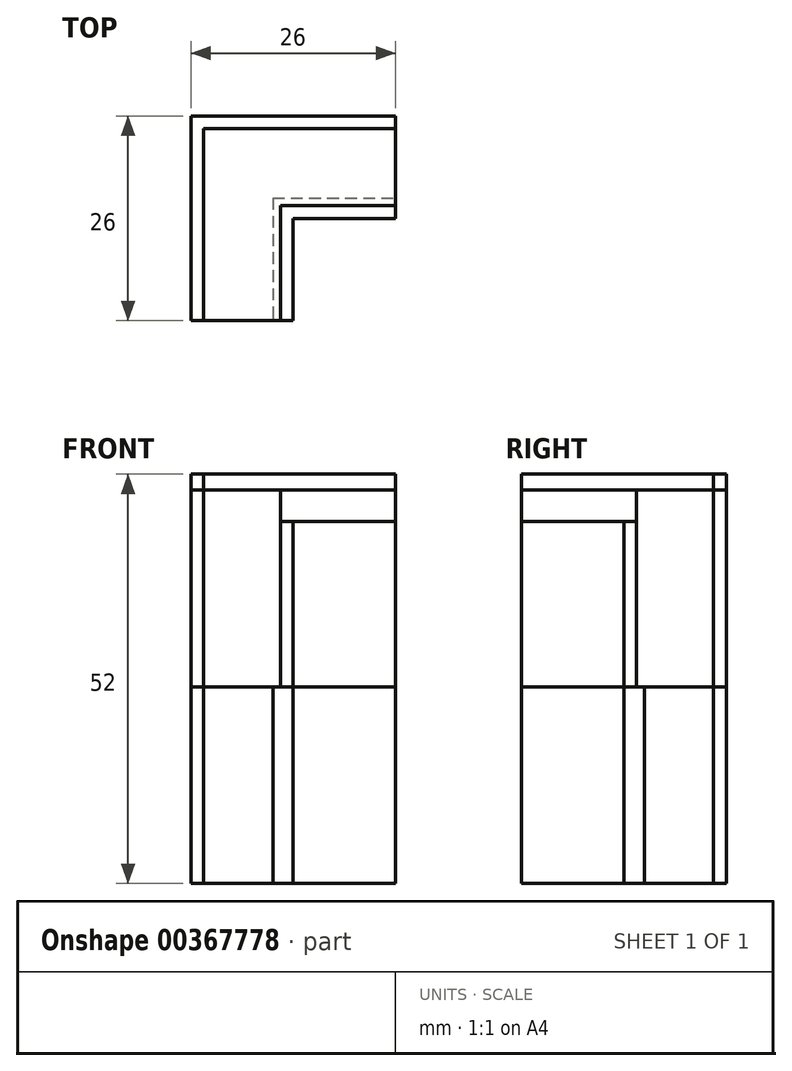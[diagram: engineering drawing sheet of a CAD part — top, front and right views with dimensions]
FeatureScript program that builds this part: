
annotation { "Feature Type Name" : "Feature", "Feature Type Description" : "" }
export const myFeature = defineFeature(function(context is Context, id is Id, definition is map)
    precondition{}
    {
        {
            var Q0;
            Q0=qCreatedBy(makeId("Top.planeOp"),FACE);
            var sketch = newSketch(context, id + "F0", { "sketchPlane" : qUnion([Q0])});
            skLineSegment(sketch, "E0.top", {"start": v(0, -13) * mm, "end": v(-13, -13) * mm});
            skLineSegment(sketch, "E0.left", {"start": v(0, 0) * mm, "end": v(0, -13) * mm});
            skLineSegment(sketch, "E0.right", {"start": v(-13, 0) * mm, "end": v(-13, -13) * mm});
            skLineSegment(sketch, "E1.top", {"start": v(0, 13) * mm, "end": v(-13, 13) * mm});
            skLineSegment(sketch, "E1.right", {"start": v(-13, 0) * mm, "end": v(-13, 13) * mm});
            skLineSegment(sketch, "E2.bottom", {"start": v(0, 0) * mm, "end": v(13, 0) * mm});
            skLineSegment(sketch, "E2.top", {"start": v(0, 13) * mm, "end": v(13, 13) * mm});
            skLineSegment(sketch, "E2.right", {"start": v(13, 0) * mm, "end": v(13, 13) * mm});
            skLineSegment(sketch, "E3.0", {"start": v(0, 10.4) * mm, "end": v(13, 10.4) * mm});
            skLineSegment(sketch, "E3.1", {"start": v(0, 10.4) * mm, "end": v(-10.4, 10.4) * mm});
            skLineSegment(sketch, "E3.2", {"start": v(-10.4, 0) * mm, "end": v(-10.4, 10.4) * mm});
            skLineSegment(sketch, "E3.3", {"start": v(-10.4, 0) * mm, "end": v(-10.4, -13) * mm});
            skLineSegment(sketch, "E4.0", {"start": v(-2.6, 2.6) * mm, "end": v(-2.6, -13) * mm});
            skLineSegment(sketch, "E4.1", {"start": v(-2.6, 2.6) * mm, "end": v(13, 2.6) * mm});
            skLineSegment(sketch, "E5.0", {"start": v(-1.6, 1.6) * mm, "end": v(-1.6, -13) * mm});
            skLineSegment(sketch, "E5.1", {"start": v(-1.6, 1.6) * mm, "end": v(13, 1.6) * mm});
            skLineSegment(sketch, "E6.0", {"start": v(-11.4, 0) * mm, "end": v(-11.4, -13) * mm});
            skLineSegment(sketch, "E6.1", {"start": v(-11.4, 0) * mm, "end": v(-11.4, 11.4) * mm});
            skLineSegment(sketch, "E6.2", {"start": v(0, 11.4) * mm, "end": v(-11.4, 11.4) * mm});
            skLineSegment(sketch, "E6.3", {"start": v(0, 11.4) * mm, "end": v(13, 11.4) * mm});
            skSolve(sketch);
        }
        {
            var Q0;
            {var subQ1=sQuery(id+"F0.wireOp",EDGE,"E0.right");Q0=makeQuery(id+"F0.imprint","IMPRINT",FACE,{"disambiguationData":[TD([[makeQuery(id+"F0.imprint","IMPRINT",EDGE,{"derivedFrom":subQ1}),1.0]])]});}
            var Q1;
            {var subQ1=sQuery(id+"F0.wireOp",EDGE,"E4.0");Q1=makeQuery(id+"F0.imprint","IMPRINT",FACE,{"disambiguationData":[TD([[makeQuery(id+"F0.imprint","IMPRINT",EDGE,{"derivedFrom":subQ1}),1.0]])]});}
            var Q2;
            {var subQ1=sQuery(id+"F0.wireOp",EDGE,"E0.left");Q2=makeQuery(id+"F0.imprint","IMPRINT",FACE,{"disambiguationData":[TD([[makeQuery(id+"F0.imprint","IMPRINT",EDGE,{"derivedFrom":subQ1}),-1.0]])]});}
            extrude(context, id + "F1", {"entities" : qUnion([Q0, Q1, Q2]), "depth" : -25 * mm});
        }
        {
            var Q0;
            {var subQ1=sQuery(id+"F0.wireOp",EDGE,"E0.left");Q0=makeQuery(id+"F0.imprint","IMPRINT",FACE,{"disambiguationData":[TD([[makeQuery(id+"F0.imprint","IMPRINT",EDGE,{"derivedFrom":subQ1}),-1.0]])]});}
            extrude(context, id + "F2", {"entities" : qUnion([Q0]), "depth" : 21 * mm});
        }
        {
            var Q0;
            {var subQ0=sQuery(id+"F0.wireOp",EDGE,"E0.right");Q0=makeQuery(id+"F0.imprint","IMPRINT",FACE,{"disambiguationData":[TD([[makeQuery(id+"F0.imprint","IMPRINT",EDGE,{"derivedFrom":subQ0}),1.0]])]});}
            extrude(context, id + "F3", {"entities" : qUnion([Q0]), "depth" : 27 * mm});
        }
        {
            var Q0;
            {var subQ0=sQuery(id+"F0.wireOp",EDGE,"E0.right");Q0=makeQuery(id+"F0.imprint","IMPRINT",FACE,{"disambiguationData":[TD([[makeQuery(id+"F0.imprint","IMPRINT",EDGE,{"derivedFrom":subQ0}),1.0]])]});}
            var Q1;
            {var subQ0=sQuery(id+"F0.wireOp",EDGE,"E3.0");Q1=makeQuery(id+"F0.imprint","IMPRINT",FACE,{"disambiguationData":[TD([[makeQuery(id+"F0.imprint","IMPRINT",EDGE,{"derivedFrom":subQ0}),1.0]])]});}
            var Q2;
            {var subQ0=sQuery(id+"F0.wireOp",EDGE,"E3.0");Q2=makeQuery(id+"F0.imprint","IMPRINT",FACE,{"disambiguationData":[TD([[makeQuery(id+"F0.imprint","IMPRINT",EDGE,{"derivedFrom":subQ0}),-1.0]])]});}
            var Q3;
            {var subQ0=sQuery(id+"F0.wireOp",EDGE,"E4.0");Q3=makeQuery(id+"F0.imprint","IMPRINT",FACE,{"disambiguationData":[TD([[makeQuery(id+"F0.imprint","IMPRINT",EDGE,{"derivedFrom":subQ0}),1.0]])]});}
            extrude(context, id + "F4", {"entities" : qUnion([Q0, Q1, Q2, Q3]), "depth" : 25 * mm});
        }
    });
